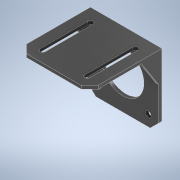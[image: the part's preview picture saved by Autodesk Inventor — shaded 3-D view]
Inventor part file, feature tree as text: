
AUTODESK INVENTOR PART (.ipt)
format: ipt  version: 2022 (Build 260153000, 153)  size: 185,344 bytes
history: native  units: mm
features: extrude x5, sketch x5, chamfer x2, projected_geometry x1
ambient origin geometry x8: Origin, YZ Plane, XZ Plane, XY Plane, X Axis, Y Axis, Z Axis, Center Point
bodies: Solid1 (feature_tree)
feature tree (13):
  extrude  "Extrusion1"  Depth=10.0mm
  extrude  "Extrusion2"  Depth=10.0mm
  chamfer  "Chamfer1"  Distance=8.0mm
  chamfer  "Chamfer2"  Distance=3.0mm
  extrude  "Extrusion3"  Depth=3.0mm
  extrude  "Extrusion4"  Depth=65.0mm TaperAngle=0.0deg
  extrude  "Extrusion5"  Depth=2.5mm TaperAngle=45.0deg
  sketch  "Sketch1"  dims[d0=10.0mm d1=10.0mm]
  sketch  "Sketch2"  dims[d2=10.0mm d3=10.0mm]
  sketch  "Sketch3"  dims[d4=8.0mm]
  sketch  "Sketch4"  dims[d5=8.0mm]
  projected_geometry  "Projected Loop1"
  sketch  "Sketch5"  dims[d6=8.0mm d7=8.0mm d8=3.0mm d9=0.0mm d10=3.0mm d11=65.0mm d12=0.0mm d13=8.0mm d14=2.0mm d15=45.0deg d16=8.0mm d17=2.0mm d18=45.0deg d19=25.0mm d20=16.0mm d21=3.0mm d22=0.0mm d23=3.0mm d24=0.0mm d25=10.0mm d26=5.0mm d27=50.0mm d28=10.0mm d29=5.0mm d30=2.5mm d31=0.0mm d32=0.0mm]
